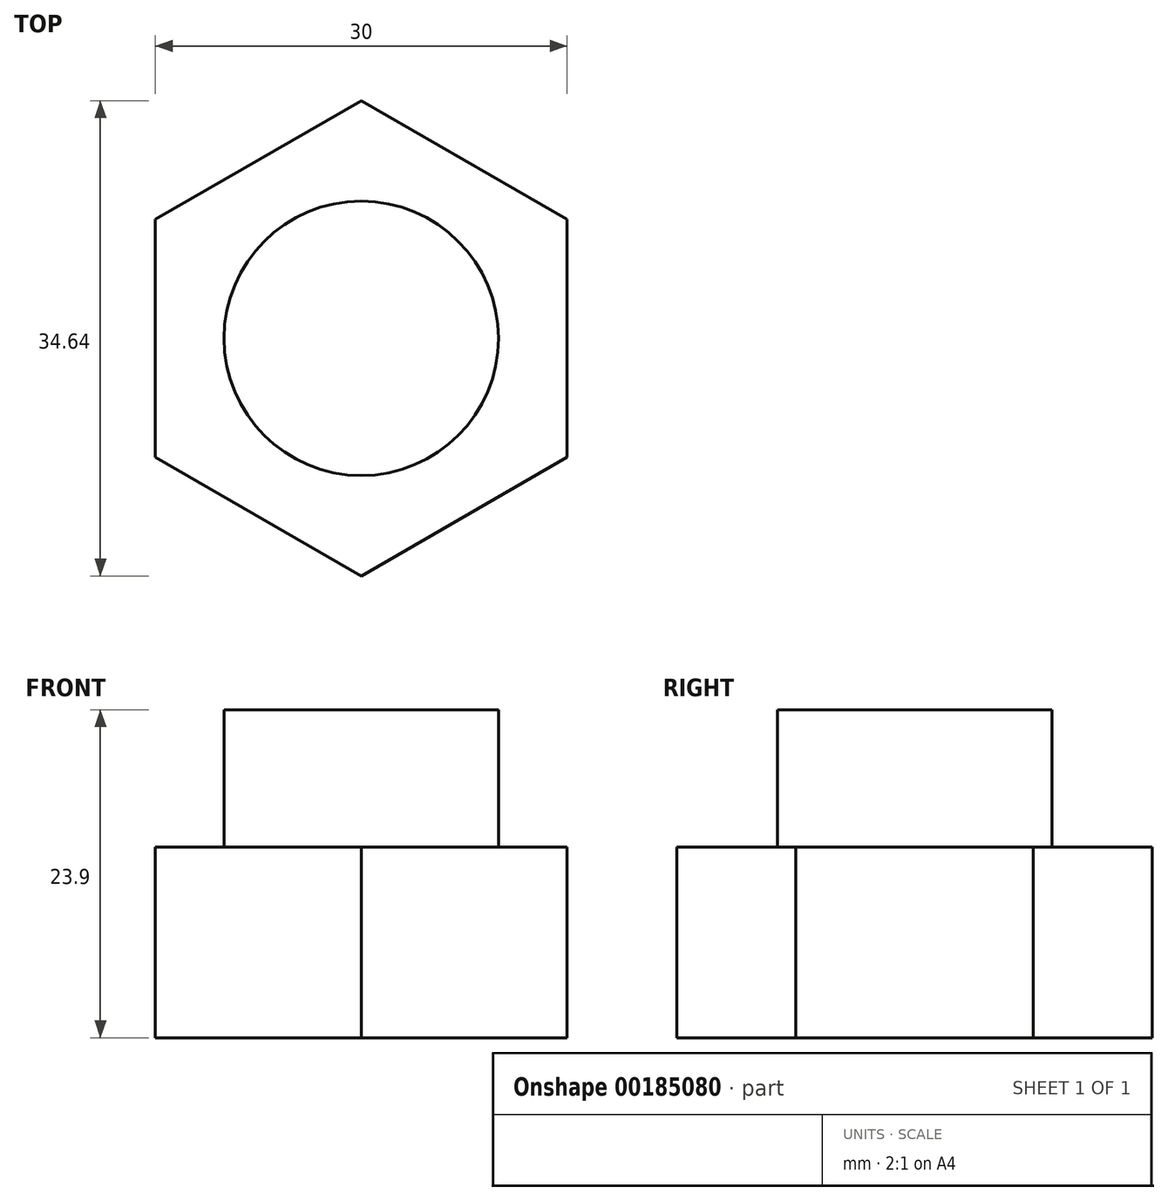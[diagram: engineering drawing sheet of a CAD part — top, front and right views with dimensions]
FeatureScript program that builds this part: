
annotation { "Feature Type Name" : "Feature", "Feature Type Description" : "" }
export const myFeature = defineFeature(function(context is Context, id is Id, definition is map)
    precondition{}
    {
        {
            var Q0;
            Q0=qCreatedBy(makeId("Top.planeOp"),FACE);
            var sketch = newSketch(context, id + "F0", { "sketchPlane" : qUnion([Q0])});
            skCircle(sketch, "E0.cCircle", {"center": v(0, 0) * mm, "radius": 17.32 * mm, "construction": true});
            skLineSegment(sketch, "E0.0", {"start": v(0, 17.32) * mm, "end": v(15, 8.66) * mm});
            skLineSegment(sketch, "E0.1", {"start": v(15, 8.66) * mm, "end": v(15, -8.66) * mm});
            skLineSegment(sketch, "E0.2", {"start": v(15, -8.66) * mm, "end": v(0, -17.32) * mm});
            skLineSegment(sketch, "E0.3", {"start": v(0, -17.32) * mm, "end": v(-15, -8.66) * mm});
            skLineSegment(sketch, "E0.4", {"start": v(-15, -8.66) * mm, "end": v(-15, 8.66) * mm});
            skLineSegment(sketch, "E0.5", {"start": v(-15, 8.66) * mm, "end": v(0, 17.32) * mm});
            skSolve(sketch);
        }
        {
            var Q0;
            Q0=makeQuery(id+"F0.imprint","IMPRINT",FACE,{"disambiguationData":[TD([[makeQuery(id+"F0.imprint","IMPRINT",EDGE,{"derivedFrom":sQuery(id+"F0.wireOp",EDGE,"E0.0")}),-1.0]])]});
            extrude(context, id + "F1", {"entities" : qUnion([Q0]), "depth" : 13.9 * mm});
        }
        {
            var Q0;
            Q0=makeQuery(id+"F1.opExtrude","CAP_FACE",FACE,{"disambiguationData":[OSD([sQuery(id+"F0.wireOp",EDGE,"E0.0"),sQuery(id+"F0.wireOp",EDGE,"E0.1"),sQuery(id+"F0.wireOp",EDGE,"E0.2"),sQuery(id+"F0.wireOp",EDGE,"E0.3"),sQuery(id+"F0.wireOp",EDGE,"E0.4"),sQuery(id+"F0.wireOp",EDGE,"E0.5")])],"isStart":false});
            var sketch = newSketch(context, id + "F2", { "sketchPlane" : qUnion([Q0])});
            skCircle(sketch, "E1", {"center": v(0, 0) * mm, "radius": 10 * mm});
            skSolve(sketch);
        }
        {
            var Q0;
            Q0=makeQuery(id+"F2.imprint","IMPRINT",FACE,{"disambiguationData":[TD([[makeQuery(id+"F2.imprint","IMPRINT",EDGE,{"derivedFrom":sQuery(id+"F2.wireOp",EDGE,"E1")}),1.0]])]});
            extrude(context, id + "F3", {"entities" : qUnion([Q0]), "operationType" : NewBodyOperationType.ADD, "depth" : 10 * mm});
        }
        {
            var Q0;
            Q0=makeQuery(id+"F1.opExtrude","CAP_EDGE",EDGE,{"disambiguationData":[OSD([sQuery(id+"F0.wireOp",EDGE,"E0.2")])],"isStart":true});
            var Q1;
            Q1=makeQuery(id+"F1.opExtrude","CAP_EDGE",EDGE,{"disambiguationData":[OSD([sQuery(id+"F0.wireOp",EDGE,"E0.2")])],"isStart":false});
            revolve(context, id + "F4", {"bodyType" : ToolBodyType.SURFACE, "surfaceEntities" : qUnion([Q0]), "axis" : qUnion([Q1]), "revolveType" : RevolveType.ONE_DIRECTION, "oppositeDirection" : true, "angle" : 30 * degree});
        }
    });
